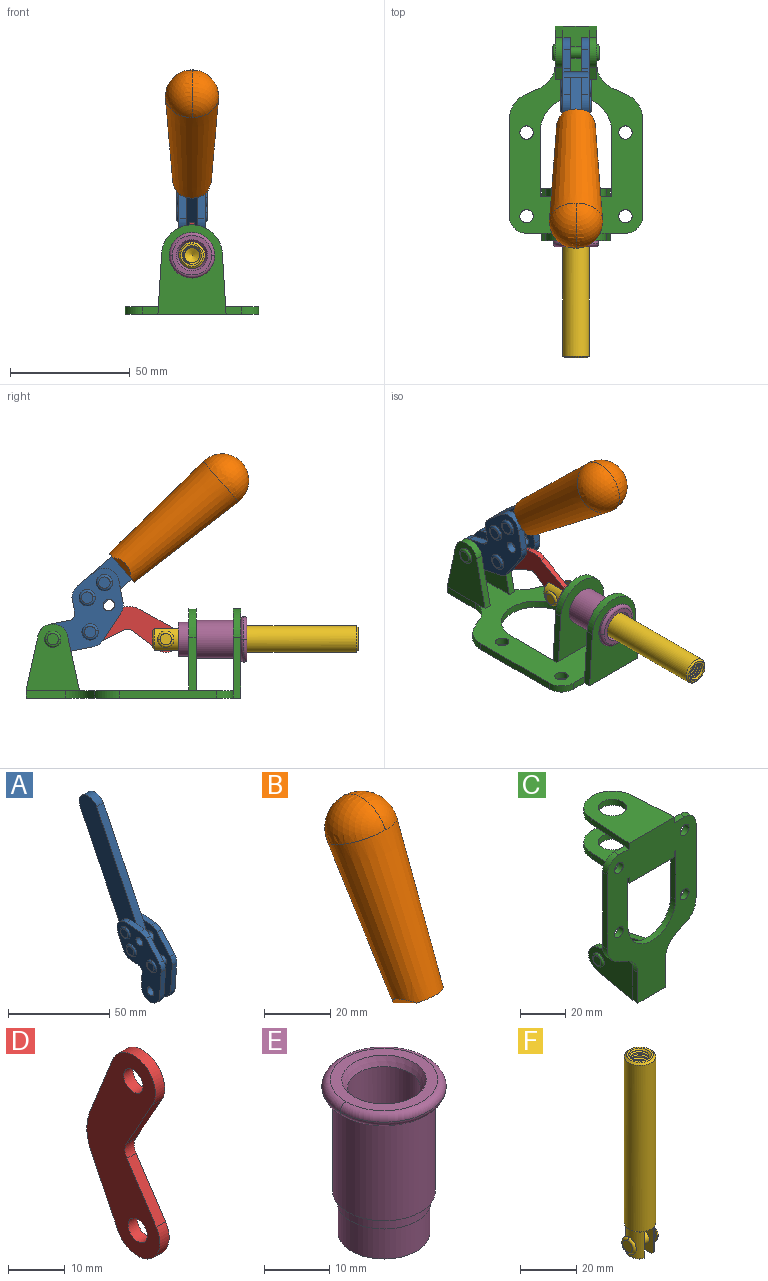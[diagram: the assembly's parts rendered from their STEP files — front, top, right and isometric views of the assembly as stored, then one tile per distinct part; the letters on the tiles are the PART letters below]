
ASSEMBLY  parts=6 mates=6
PART A: 59 faces, bbox 12.9x60.2x99.6 mm
  f0: torus R=2.39mm, axis (-1,0,0), area 14.9mm2, adj f20,f43,f51
  f1: torus R=2.39mm, axis (-1,0,0), area 14.9mm2, adj f19,f42,f51
  f2: torus R=2.39mm, axis (-1,0,0), area 14.9mm2, adj f18,f35,f51
  f3: torus R=2.39mm, axis (-1,0,0), area 14.9mm2, adj f14,f17,f23
  f4: torus R=2.39mm, axis (-1,0,0), area 14.9mm2, adj f13,f16,f23
  f5: torus R=2.39mm, axis (-1,0,0), area 14.9mm2, adj f12,f15,f23
  f6: cylinder r=2.39mm len=4.78mm, axis (1,0,0), area 46.5mm2, adj f48,f50,f51
  f7: cylinder r=2.39mm len=4.78mm, axis (1,0,0), area 46.5mm2, adj f50,f51
  f8: cylinder r=6.35mm len=12.68mm, axis (1,0,0), area 61.8mm2, adj f38,f39,f50,f51
  f9: cylinder r=2.39mm len=4.78mm, axis (-1,0,0), area 70.5mm2, adj f46,f50
  f10: cylinder r=2.39mm len=4.78mm, axis (-1,0,0), area 46.5mm2, adj f23,f45,f46
  f11: cylinder r=2.39mm len=4.78mm, axis (-1,0,0), area 46.5mm2, adj f23,f46
  f12: plane 4.78x4.78mm, normal (1,0,0), area 17.9mm2, adj f5,f15
  f13: plane 4.78x4.78mm, normal (1,0,0), area 17.9mm2, adj f4,f16
  f14: plane 4.78x4.78mm, normal (1,0,0), area 17.9mm2, adj f3,f17
  f15: torus R=2.39mm, axis (-1,0,0), area 14.9mm2, adj f5,f12,f23
  f16: torus R=2.39mm, axis (-1,0,0), area 14.9mm2, adj f4,f13,f23
  f17: torus R=2.39mm, axis (-1,0,0), area 14.9mm2, adj f3,f14,f23
  f18: plane 4.78x4.78mm, normal (-1,0,0), area 17.9mm2, adj f2,f35
  f19: plane 4.78x4.78mm, normal (-1,0,0), area 17.9mm2, adj f1,f42
  f20: plane 4.78x4.78mm, normal (-1,0,0), area 17.9mm2, adj f0,f43
  f21: plane 2.26x0.2mm, normal (1,0,0), area 0.2mm2, adj f31,f44
  f22: plane 2.26x0.2mm, normal (-1,0,0), area 0.2mm2, adj f41,f44
  f23: plane 39.37x30.77mm, normal (1,0,0), area 565.5mm2, adj f3,f4,f5,f10,f11,f15,f16,f17
  f24: cylinder r=6.1mm len=4.15mm, axis (-1,0,0), area 14.7mm2, adj f23,f25,f32,f46
  f25: plane 10.25x9.01mm, normal (0,-0.75,0.66), area 42.3mm2, adj f23,f24,f26,f46
  f26: cylinder r=6.35mm len=4.64mm, axis (-1,0,0), area 15.6mm2, adj f23,f25,f27,f46
  f27: plane 15.84x3.1mm, normal (0,-1,-0.07), area 49.2mm2, adj f23,f26,f28,f46
  f28: cylinder r=6.35mm len=12.68mm, axis (-1,0,0), area 61.8mm2, adj f23,f27,f29,f46
  f29: plane 8.11x3.1mm, normal (0,1,0.07), area 25.2mm2, adj f23,f28,f30,f46
  f30: cylinder r=3.05mm len=3.25mm, axis (-1,0,0), area 14.8mm2, adj f23,f29,f31,f46
  f31: plane 5.99x3.1mm, normal (0,0.07,-1), area 18.6mm2, adj f21,f23,f30,f44,f46
  f32: plane 9.5x3.1mm, normal (0,-0.07,1), area 29.5mm2, adj f23,f24,f33,f46,f47
  f33: cylinder r=6.1mm len=8.63mm, axis (-1,0,0), area 39.1mm2, adj f23,f32,f34,f47
  f34: plane 8.65x3.96mm, normal (0,0.91,-0.42), area 29.5mm2, adj f23,f33,f44,f47
  f35: torus R=2.39mm, axis (-1,0,0), area 14.9mm2, adj f2,f18,f51
  f36: plane 10.25x9.01mm, normal (0,-0.75,0.66), area 42.3mm2, adj f37,f49,f50,f51
  f37: cylinder r=6.35mm len=4.64mm, axis (1,0,0), area 15.6mm2, adj f36,f38,f50,f51
  f38: plane 15.84x3.1mm, normal (0,-1,-0.07), area 49.2mm2, adj f8,f37,f50,f51
  f39: plane 8.11x3.1mm, normal (0,1,0.07), area 25.2mm2, adj f8,f40,f50,f51
  f40: cylinder r=3.05mm len=3.25mm, axis (1,0,0), area 14.8mm2, adj f39,f41,f50,f51
  f41: plane 5.99x3.1mm, normal (0,0.07,-1), area 18.6mm2, adj f22,f40,f44,f50,f51
  f42: torus R=2.39mm, axis (-1,0,0), area 14.9mm2, adj f1,f19,f51
  f43: torus R=2.39mm, axis (-1,0,0), area 14.9mm2, adj f0,f20,f51
  f44: cylinder r=6.35mm len=12.12mm, axis (-1,0,0), area 128.9mm2, adj f21,f22,f23,f31,f34,f41,f46,f47
  f45: plane 2.65x1.35mm, normal (1,0,0), area 1mm2, adj f10,f55
  f46: plane 39.08x20.42mm, normal (-1,0,0), area 412.5mm2, adj f9,f10,f11,f24,f25,f26,f27,f28
  f47: plane 77.62x39.82mm, normal (1,0,0), area 850mm2, adj f32,f33,f34,f44,f53,f54,f55
  f48: plane 2.65x1.35mm, normal (-1,0,0), area 1mm2, adj f6,f55
  f49: cylinder r=6.1mm len=4.15mm, axis (1,0,0), area 14.7mm2, adj f36,f50,f51,f56
  f50: plane 39.08x20.42mm, normal (1,0,0), area 412.5mm2, adj f6,f7,f8,f9,f36,f37,f38,f39
  f51: plane 39.37x30.77mm, normal (-1,0,0), area 565.5mm2, adj f0,f1,f2,f6,f7,f8,f35,f36
  f52: plane 8.65x3.96mm, normal (0,0.91,-0.42), area 29.5mm2, adj f44,f51,f57,f58
  f53: plane 68.49x33.4mm, normal (0,0.9,-0.44), area 358.1mm2, adj f44,f47,f54,f58
  f54: cylinder r=6.35mm len=12.06mm, axis (1,0,0), area 93.7mm2, adj f47,f53,f55,f58
  f55: plane 68.49x33.4mm, normal (0,-0.9,0.44), area 358.1mm2, adj f44,f45,f46,f47,f48,f50,f54,f58
  f56: plane 9.5x3.1mm, normal (0,-0.07,1), area 29.5mm2, adj f49,f50,f51,f57,f58
  f57: cylinder r=6.1mm len=8.63mm, axis (1,0,0), area 39.1mm2, adj f51,f52,f56,f58
  f58: plane 77.62x39.82mm, normal (-1,0,0), area 850mm2, adj f44,f52,f53,f54,f55,f56,f57
PART B: 11 faces, bbox 22.3x42.6x64.5 mm
  f0: sphere r=11.13mm, area 411.4mm2, adj f1,f8
  f1: cone r=11.11mm half-angle=3.3deg, axis (0,0.44,0.9), area 3251.8mm2, adj f0,f7,f8,f9,f10
  f2: cylinder r=6.16mm len=11.7mm, axis (1,0,0), area 89.5mm2, adj f3,f4,f5,f6
  f3: plane 60.23x36.75mm, normal (-1,0,0), area 763.6mm2, adj f2,f4,f6,f10
  f4: plane 51.37x25.05mm, normal (0,0.9,-0.44), area 264.2mm2, adj f2,f3,f5,f10
  f5: plane 60.23x36.75mm, normal (1,0,0), area 763.6mm2, adj f2,f4,f6,f10
  f6: plane 51.37x25.05mm, normal (0,-0.9,0.44), area 264.2mm2, adj f2,f3,f5,f10
  f7: plane 9.95x5.95mm, normal (0.71,-0.31,-0.64), area 25.8mm2, adj f1,f10
  f8: sphere r=11.13mm, area 411.4mm2, adj f0,f1
  f9: plane 9.95x5.95mm, normal (-0.71,-0.31,-0.64), area 25.8mm2, adj f1,f10
  f10: plane 14.27x11.38mm, normal (0,-0.44,-0.9), area 106.7mm2, adj f1,f3,f4,f5,f6,f7,f9
PART C: 55 faces, bbox 55.7x37.4x89.8 mm
  f0: torus R=2.41mm, axis (-1,0,0), area 15mm2, adj f11,f15,f25
  f1: torus R=2.41mm, axis (-1,0,0), area 15mm2, adj f10,f12,f22
  f2: cylinder r=2.78mm len=5.56mm, axis (0,-1,0), area 54.2mm2, adj f30,f54
  f3: cylinder r=14.99mm len=29.97mm, axis (0,-1,0), area 145.9mm2, adj f30,f49,f53,f54
  f4: cylinder r=2.78mm len=5.56mm, axis (0,-1,0), area 54.2mm2, adj f30,f54
  f5: cylinder r=2.78mm len=5.56mm, axis (0,-1,0), area 54.2mm2, adj f30,f54
  f6: cylinder r=2.78mm len=5.56mm, axis (0,-1,0), area 54.2mm2, adj f30,f54
  f7: cylinder r=6.35mm len=12.7mm, axis (0,0,1), area 123.6mm2, adj f27,f51
  f8: cylinder r=6.35mm len=12.7mm, axis (0,0,-1), area 124.7mm2, adj f21,f35
  f9: cylinder r=2.41mm len=11.18mm, axis (-1,0,0), area 169.4mm2, adj f16,f19
  f10: plane 4.83x4.83mm, normal (1,0,0), area 18.3mm2, adj f1,f12
  f11: plane 4.83x4.83mm, normal (-1,0,0), area 18.3mm2, adj f0,f15
  f12: torus R=2.41mm, axis (-1,0,0), area 15mm2, adj f1,f10,f22
  f13: cylinder r=6.35mm len=12.41mm, axis (1,0,0), area 53.4mm2, adj f18,f19,f22,f23
  f14: cylinder r=6.35mm len=12.41mm, axis (-1,0,0), area 53.4mm2, adj f16,f17,f24,f25
  f15: torus R=2.41mm, axis (-1,0,0), area 15mm2, adj f0,f11,f25
  f16: plane 27.86x22.35mm, normal (1,0,0), area 425.4mm2, adj f9,f14,f17,f24,f30
  f17: plane 22.86x4.97mm, normal (0,0.21,0.98), area 72.5mm2, adj f14,f16,f25,f30
  f18: plane 22.86x4.97mm, normal (0,0.21,0.98), area 72.5mm2, adj f13,f19,f22,f30
  f19: plane 27.86x22.35mm, normal (-1,0,0), area 425.4mm2, adj f9,f13,f18,f23,f30
  f20: cylinder r=12.7mm len=25.35mm, axis (0,0,-1), area 119.8mm2, adj f21,f34,f35,f36
  f21: plane 34.21x28.07mm, normal (0,0,-1), area 702.4mm2, adj f8,f20,f30,f34,f36
  f22: plane 27.96x22.45mm, normal (1,0,0), area 407.2mm2, adj f1,f12,f13,f18,f23,f30,f42,f43
  f23: plane 22.86x4.97mm, normal (0,0.21,-0.98), area 72.5mm2, adj f13,f19,f22,f44
  f24: plane 22.86x4.97mm, normal (0,0.21,-0.98), area 72.5mm2, adj f14,f16,f25,f44
  f25: plane 27.86x22.35mm, normal (-1,0,0), area 407.1mm2, adj f0,f14,f15,f17,f24,f30,f45,f46
  f26: plane 3.1x0.95mm, normal (0,0,-1), area 2.7mm2, adj f30,f49,f50,f54
  f27: plane 34.21x28.07mm, normal (0,0,1), area 702.4mm2, adj f7,f28,f30,f50,f52
  f28: cylinder r=12.7mm len=25.35mm, axis (0,0,1), area 118.8mm2, adj f27,f50,f51,f52
  f29: plane 3.1x0.95mm, normal (0,0,-1), area 2.7mm2, adj f30,f52,f53,f54
  f30: plane 86.54x55.63mm, normal (0,1,0), area 2362.9mm2, adj f2,f3,f4,f5,f6,f16,f17,f18
  f31: plane 40.56x3.1mm, normal (-1,0,0), area 125.7mm2, adj f30,f32,f48,f54
  f32: cylinder r=7.11mm len=7.11mm, axis (0,-1,0), area 34.6mm2, adj f30,f31,f33,f54
  f33: plane 6.67x3.1mm, normal (0,0,1), area 20.4mm2, adj f30,f32,f34,f54
  f34: plane 25.39x3.13mm, normal (-1,0.06,0), area 79.5mm2, adj f20,f21,f33,f35,f54
  f35: plane 37.31x28.45mm, normal (0,0,1), area 789.9mm2, adj f8,f20,f34,f36,f54
  f36: plane 25.39x3.13mm, normal (1,0.06,0), area 79.5mm2, adj f20,f21,f35,f37,f54
  f37: plane 6.67x3.1mm, normal (0,0,1), area 20.4mm2, adj f30,f36,f38,f54
  f38: cylinder r=7.11mm len=7.11mm, axis (0,-1,0), area 34.6mm2, adj f30,f37,f39,f54
  f39: plane 40.56x3.1mm, normal (1,0,0), area 125.7mm2, adj f30,f38,f40,f54
  f40: cylinder r=11.18mm len=10.16mm, axis (0,-1,0), area 39.5mm2, adj f30,f39,f41,f54
  f41: plane 6.09x3.1mm, normal (0.42,0,-0.91), area 20.8mm2, adj f30,f40,f42,f54
  f42: cylinder r=11.18mm len=9.41mm, axis (0,-1,0), area 37.2mm2, adj f22,f30,f41,f43,f54
  f43: plane 16.5x3.1mm, normal (1,0,0), area 51.1mm2, adj f22,f42,f44,f54
  f44: plane 17.37x3.1mm, normal (0,0,-1), area 53.8mm2, adj f23,f24,f30,f43,f45,f54
  f45: plane 16.5x3.1mm, normal (-1,0,0), area 51.1mm2, adj f25,f44,f46,f54
  f46: cylinder r=11.18mm len=9.41mm, axis (0,-1,0), area 37.2mm2, adj f25,f30,f45,f47,f54
  f47: plane 6.09x3.1mm, normal (-0.42,0,-0.91), area 20.8mm2, adj f30,f46,f48,f54
  f48: cylinder r=11.18mm len=10.16mm, axis (0,-1,0), area 39.5mm2, adj f30,f31,f47,f54
  f49: plane 26.54x3.1mm, normal (-1,0,0), area 82.3mm2, adj f3,f26,f30,f54
  f50: plane 25.39x3.1mm, normal (1,0.06,0), area 78.8mm2, adj f26,f27,f28,f51,f54
  f51: plane 37.31x28.45mm, normal (0,0,-1), area 789.9mm2, adj f7,f28,f50,f52,f54
  f52: plane 25.39x3.1mm, normal (-1,0.06,0), area 78.8mm2, adj f27,f28,f29,f51,f54
  f53: plane 26.54x3.1mm, normal (1,0,0), area 82.3mm2, adj f3,f29,f30,f54
  f54: plane 89.66x55.63mm, normal (0,-1,0), area 2678.5mm2, adj f2,f3,f4,f5,f6,f26,f29,f31
PART D: 12 faces, bbox 2.3x18.2x42.8 mm
  f0: cylinder r=2.4mm len=4.8mm, axis (1,0,0), area 34.9mm2, adj f4,f11
  f1: cylinder r=10.41mm len=8.47mm, axis (1,0,0), area 20.2mm2, adj f4,f9,f10,f11
  f2: cylinder r=3.05mm len=3.16mm, axis (1,0,0), area 7.7mm2, adj f4,f6,f7,f11
  f3: cylinder r=2.4mm len=4.8mm, axis (1,0,0), area 34.9mm2, adj f4,f11
  f4: plane 42.81x18.23mm, normal (-1,0,0), area 414.1mm2, adj f0,f1,f2,f3,f5,f6,f7,f8
  f5: cylinder r=5.54mm len=10.67mm, axis (1,0,0), area 41.8mm2, adj f4,f6,f10,f11
  f6: plane 11.66x6.53mm, normal (0,-0.87,-0.49), area 30.9mm2, adj f2,f4,f5,f11
  f7: plane 11.17x7.33mm, normal (0,-0.84,0.55), area 30.9mm2, adj f2,f4,f8,f11
  f8: cylinder r=5.54mm len=10.51mm, axis (1,0,0), area 41.8mm2, adj f4,f7,f9,f11
  f9: plane 13.67x6.67mm, normal (0,0.9,-0.44), area 35.1mm2, adj f1,f4,f8,f11
  f10: plane 14.1x5.7mm, normal (0,0.93,0.37), area 35.1mm2, adj f1,f4,f5,f11
  f11: plane 42.81x18.23mm, normal (1,0,0), area 414.1mm2, adj f0,f1,f2,f3,f5,f6,f7,f8
PART E: 15 faces, bbox 20.6x20.6x28.7 mm
  f0: torus R=8.26mm, axis (0,0,1), area 56.8mm2, adj f1,f10,f12
  f1: torus R=8.26mm, axis (0,0,1), area 56.8mm2, adj f0,f6,f13
  f2: cylinder r=5.59mm len=25.91mm, axis (0,0,1), area 909.6mm2, adj f3,f4
  f3: cone r=6.86mm half-angle=45deg, axis (0,0,-1), area 70.2mm2, adj f2,f14
  f4: cone r=6.47mm half-angle=30deg, axis (0,0,1), area 66.7mm2, adj f2,f13
  f5: cylinder r=7.04mm len=14.07mm, axis (0,0,1), area 252.6mm2, adj f11,f14
  f6: torus R=8.26mm, axis (0,0,1), area 56.8mm2, adj f1,f12,f13
  f7: cylinder r=7.16mm len=14.33mm, axis (0,0,1), area 91.5mm2, adj f9,f11
  f8: cylinder r=7.86mm len=18.42mm, axis (0,0,1), area 909.6mm2, adj f9,f10
  f9: plane 15.72x15.72mm, normal (0,0,-1), area 33mm2, adj f7,f8
  f10: plane 16.51x16.51mm, normal (0,0,-1), area 19.9mm2, adj f0,f8,f12
  f11: plane 14.33x14.33mm, normal (0,0,-1), area 5.7mm2, adj f5,f7
  f12: torus R=8.26mm, axis (0,0,1), area 56.8mm2, adj f0,f6,f10
  f13: plane 16.51x16.51mm, normal (0,0,1), area 82.7mm2, adj f1,f4,f6
  f14: plane 14.07x14.07mm, normal (0,0,-1), area 7.8mm2, adj f3,f5
PART F: 48 faces, bbox 12.6x11.1x86.1 mm
  f0: torus R=2.41mm, axis (-1,0,0), area 15mm2, adj f30,f32,f34
  f1: torus R=2.41mm, axis (-1,0,0), area 15mm2, adj f29,f31,f33
  f2: cylinder r=5.54mm len=72.39mm, axis (0,0,1), area 2518.5mm2, adj f3,f4,f42,f43
  f3: cone r=5.54mm half-angle=45deg, axis (0,0,1), area 7.6mm2, adj f2,f5,f41
  f4: cone r=5.54mm half-angle=45deg, axis (0,0,-1), area 34.9mm2, adj f2,f39
  f5: cylinder r=5.08mm len=11.48mm, axis (0,0,1), area 108.3mm2, adj f3,f7,f8,f41
  f6: cylinder r=2.41mm len=4.83mm, axis (-1,0,0), area 71.2mm2, adj f40,f41
  f7: cylinder r=2.41mm len=4.83mm, axis (-1,0,0), area 7.6mm2, adj f5,f34
  f8: cone r=5.08mm half-angle=45deg, axis (0,0,1), area 10.6mm2, adj f5,f37,f41
  f9: cone r=3.98mm half-angle=45deg, axis (0,0,1), area 17.6mm2, adj f27,f39,f45,f46,f47
  f10: cylinder r=2.41mm len=4.83mm, axis (-1,0,0), area 7.6mm2, adj f33,f38
  f11: cylinder r=3.2mm len=6.4mm, axis (0,0,1), area 78.4mm2, adj f12,f28,f44,f45,f47
  f12: cylinder r=3.2mm len=6.4mm, axis (0,0,1), area 10.5mm2, adj f11,f13,f45,f47
  f13: cylinder r=3.2mm len=6.4mm, axis (0,0,1), area 10.5mm2, adj f12,f14,f45,f47
  f14: cylinder r=3.2mm len=6.4mm, axis (0,0,1), area 10.5mm2, adj f13,f15,f45,f47
  f15: cylinder r=3.2mm len=6.4mm, axis (0,0,1), area 10.5mm2, adj f14,f16,f45,f47
  f16: cylinder r=3.2mm len=6.4mm, axis (0,0,1), area 10.5mm2, adj f15,f17,f45,f47
  f17: cylinder r=3.2mm len=6.4mm, axis (0,0,1), area 10.5mm2, adj f16,f18,f45,f47
  f18: cylinder r=3.2mm len=6.4mm, axis (0,0,1), area 10.5mm2, adj f17,f19,f45,f47
  f19: cylinder r=3.2mm len=6.4mm, axis (0,0,1), area 10.5mm2, adj f18,f20,f45,f47
  f20: cylinder r=3.2mm len=6.4mm, axis (0,0,1), area 10.5mm2, adj f19,f21,f45,f47
  f21: cylinder r=3.2mm len=6.4mm, axis (0,0,1), area 10.5mm2, adj f20,f22,f45,f47
  f22: cylinder r=3.2mm len=6.4mm, axis (0,0,1), area 10.5mm2, adj f21,f23,f45,f47
  f23: cylinder r=3.2mm len=6.4mm, axis (0,0,1), area 10.5mm2, adj f22,f24,f45,f47
  f24: cylinder r=3.2mm len=6.4mm, axis (0,0,1), area 10.5mm2, adj f23,f25,f45,f47
  f25: cylinder r=3.2mm len=6.4mm, axis (0,0,1), area 10.5mm2, adj f24,f26,f45,f47
  f26: cylinder r=3.2mm len=6.4mm, axis (0,0,1), area 10.5mm2, adj f25,f27,f45,f47
  f27: cylinder r=3.2mm len=6.4mm, axis (0,0,1), area 7.4mm2, adj f9,f26,f45,f47
  f28: cone r=3.2mm half-angle=60deg, axis (0,0,1), area 37.2mm2, adj f11
  f29: plane 4.83x4.83mm, normal (-1,0,0), area 18.3mm2, adj f1,f31
  f30: plane 4.83x4.83mm, normal (1,0,0), area 18.3mm2, adj f0,f32
  f31: torus R=2.41mm, axis (-1,0,0), area 15mm2, adj f1,f29,f33
  f32: torus R=2.41mm, axis (-1,0,0), area 15mm2, adj f0,f30,f34
  f33: plane 6.83x6.83mm, normal (1,0,0), area 18.3mm2, adj f1,f10,f31
  f34: plane 6.83x6.83mm, normal (-1,0,0), area 18.3mm2, adj f0,f7,f32
  f35: cone r=5.08mm half-angle=45deg, axis (0,0,1), area 10.6mm2, adj f36,f38,f40
  f36: plane 7.25x1.97mm, normal (0,0,-1), area 10mm2, adj f35,f40
  f37: plane 7.25x1.97mm, normal (0,0,-1), area 10mm2, adj f8,f41
  f38: cylinder r=5.08mm len=11.48mm, axis (0,0,1), area 108.3mm2, adj f10,f35,f40,f42
  f39: plane 9.55x9.55mm, normal (0,0,1), area 22mm2, adj f4,f9
  f40: plane 12.76x10.09mm, normal (1,0,0), area 95.7mm2, adj f6,f35,f36,f38,f42,f43
  f41: plane 12.76x10.09mm, normal (-1,0,0), area 95.7mm2, adj f3,f5,f6,f8,f37,f43
  f42: cone r=5.54mm half-angle=45deg, axis (0,0,1), area 7.6mm2, adj f2,f38,f40
  f43: plane 11.07x4.7mm, normal (0,0,-1), area 50.4mm2, adj f2,f40,f41
  f44: plane 0.89x0.62mm, normal (-1,0,0), area 0.3mm2, adj f11,f45,f46,f47
  f45: bspline ~24.8x7.63mm, area 266.6mm2, adj f9,f11,f12,f13,f14,f15,f16,f17
  f46: bspline ~24.87x7.63mm, area 73.6mm2, adj f9,f44,f45,f47
  f47: bspline ~24.98x7.63mm, area 272.5mm2, adj f9,f11,f12,f13,f14,f15,f16,f17
PLACE A rot(axis=(1,0,0),75deg) t=(0,4.15,9.14)mm
PLACE B rot(axis=(1,0,0),75deg) t=(0,4.15,9.14)mm
PLACE C rot(axis=(1,0,0),90deg) t=(0,9.43,0)mm fixed
PLACE D rot(axis=(1,0,0),97.5deg) t=(0,12.88,2.22)mm
PLACE E rot(axis=(1,0,0),90deg) t=(0,9.43,0)mm
PLACE F rot(axis=(1,0,0),90deg) t=(0,9.81,0)mm
MATE slider F.f2 <-> E.f2  axis (0,-1,0) through (0,-48.97,24.61)mm
MATE revolute A.f4 <-> D.f3  axis (-1,0,0) through (0,25.94,27.64)mm
MATE fastened B.f2 <-> A.f54  axis (1,0,0) through (0,-30.37,91.94)mm
MATE revolute D.f5 <-> F.f6  axis (1,0,0) through (0,-5.67,24.61)mm
MATE fastened E.f0 <-> C.f7  axis (0,1,0) through (0,-36.96,24.61)mm
MATE revolute A.f7 <-> C.f0  axis (1,0,0) through (0,41.52,24.61)mm
